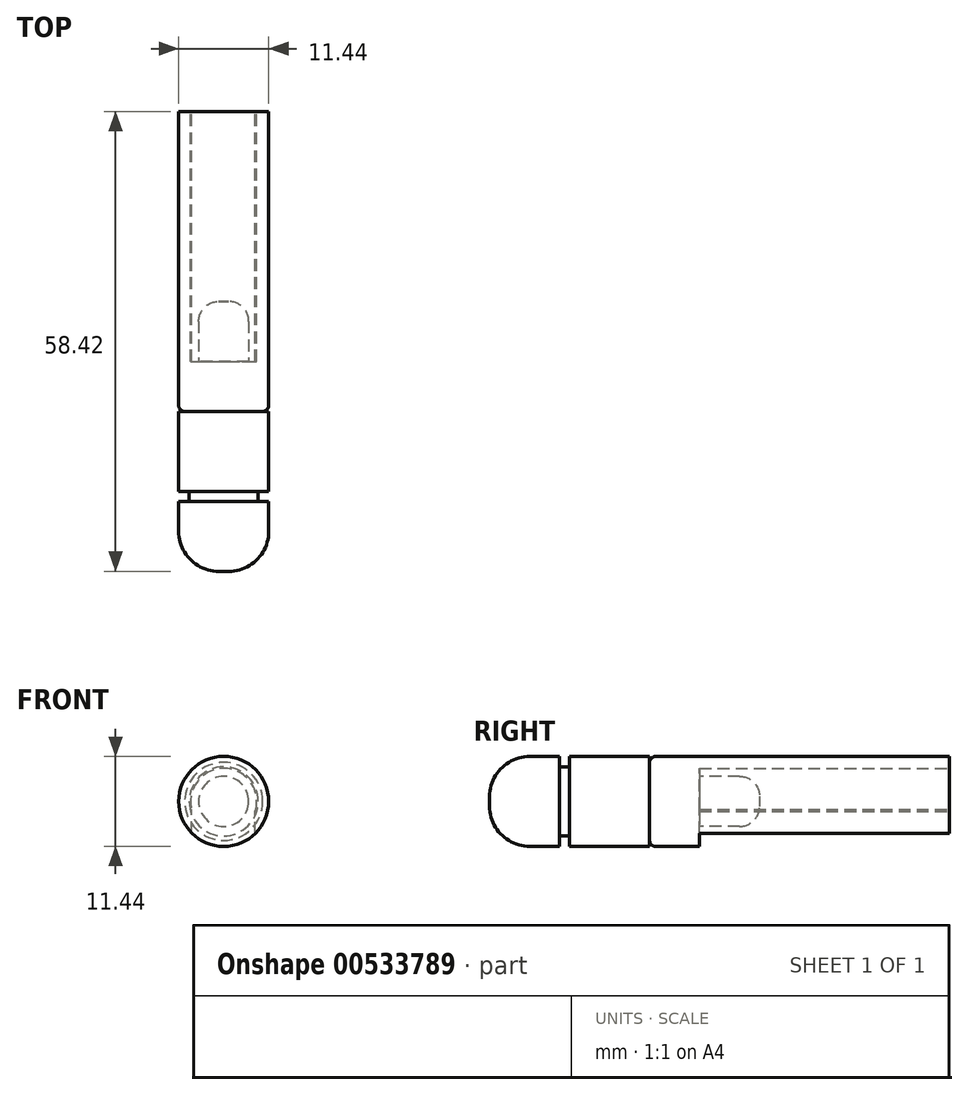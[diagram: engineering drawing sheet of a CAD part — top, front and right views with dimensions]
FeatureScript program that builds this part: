
annotation { "Feature Type Name" : "Feature", "Feature Type Description" : "" }
export const myFeature = defineFeature(function(context is Context, id is Id, definition is map)
    precondition{}
    {
        {
            var Q0;
            Q0=qCreatedBy(makeId("Front.planeOp"),FACE);
            var sketch = newSketch(context, id + "F0", { "sketchPlane" : qUnion([Q0])});
            skCircle(sketch, "E0", {"center": v(0, 0) * mm, "radius": 5.72 * mm});
            skSolve(sketch);
        }
        {
            var Q0;
            Q0=qSketchRegion(id+"F0",true);
            extrude(context, id + "F1", {"entities" : qUnion([Q0]), "depth" : 38.1 * mm, "offsetDistance" : 25.4 * mm});
        }
        {
            var Q0;
            Q0=makeQuery(id+"F1.opExtrude","CAP_FACE",FACE,{"disambiguationData":[OSD([sQuery(id+"F0.wireOp",EDGE,"E0")])],"isStart":false});
            var sketch = newSketch(context, id + "F2", { "sketchPlane" : qUnion([Q0])});
            skCircle(sketch, "E1", {"center": v(0, 0) * mm, "radius": 5.72 * mm});
            skSolve(sketch);
        }
        {
            var Q0;
            Q0=qSketchRegion(id+"F2",true);
            extrude(context, id + "F3", {"entities" : qUnion([Q0]), "depth" : 20.32 * mm, "offsetDistance" : 25.4 * mm});
        }
        {
            var Q0;
            Q0=makeQuery(id+"F1.opExtrude","CAP_EDGE",EDGE,{"disambiguationData":[OSD([sQuery(id+"F0.wireOp",EDGE,"E0")])],"isStart":false});
            fillet(context, id + "F4", {"entities" : qUnion([Q0]), "radius" : 0.76 * mm, "tangentPropagation" : true, "allowEdgeOverflow" : false});
        }
        {
            var Q0;
            Q0=makeQuery(id+"F1.opExtrude","CAP_FACE",FACE,{"disambiguationData":[OSD([sQuery(id+"F0.wireOp",EDGE,"E0")])],"isStart":true});
            var sketch = newSketch(context, id + "F5", { "sketchPlane" : qUnion([Q0])});
            skCircle(sketch, "E2", {"center": v(0, 0) * mm, "radius": 4.2 * mm});
            skSolve(sketch);
        }
        {
            var Q0;
            Q0=makeQuery(id+"F5.imprint","IMPRINT",FACE,{"disambiguationData":[TD([[makeQuery(id+"F5.imprint","IMPRINT",EDGE,{"derivedFrom":sQuery(id+"F5.wireOp",EDGE,"E2")}),1.0]])]});
            var Q1;
            Q1=sQuery(id+"F5.wireOp",EDGE,"E2");
            extrude(context, id + "F6", {"entities" : qUnion([Q0]), "operationType" : NewBodyOperationType.REMOVE, "surfaceEntities" : qUnion([Q1]), "oppositeDirection" : true, "depth" : 31.75 * mm, "offsetDistance" : 25.4 * mm});
        }
        {
            var Q0;
            Q0=qCreatedBy(makeId("Top.planeOp"),FACE);
            var sketch = newSketch(context, id + "F7", { "sketchPlane" : qUnion([Q0])});
            skLineSegment(sketch, "E3.bottom", {"start": v(-4.07, 0) * mm, "end": v(4, 0) * mm});
            skLineSegment(sketch, "E3.top", {"start": v(-4.07, -31.75) * mm, "end": v(4, -31.75) * mm});
            skLineSegment(sketch, "E3.left", {"start": v(-4.07, 0) * mm, "end": v(-4.07, -31.75) * mm});
            skLineSegment(sketch, "E3.right", {"start": v(4, 0) * mm, "end": v(4, -31.75) * mm});
            skSolve(sketch);
        }
        {
            var Q0;
            Q0=qSketchRegion(id+"F7",true);
            extrude(context, id + "F8", {"entities" : qUnion([Q0]), "operationType" : NewBodyOperationType.REMOVE, "oppositeDirection" : true, "depth" : 25.4 * mm, "offsetDistance" : 25.4 * mm});
        }
        {
            var Q0;
            Q0=makeQuery(id+"F8.boolean.opBoolean","MERGE",FACE,{"derivedFrom":[makeQuery(id+"F6.boolean.opBoolean","COPY",FACE,{"derivedFrom":makeQuery(id+"F6.opExtrude","CAP_FACE",FACE,{"disambiguationData":[OSD([sQuery(id+"F5.wireOp",EDGE,"E2")])],"isStart":false})}),makeQuery(id+"F8.opExtrude","SWEPT_FACE",FACE,{"disambiguationData":[OSD([sQuery(id+"F7.wireOp",EDGE,"E3.top")])]})]});
            var sketch = newSketch(context, id + "F9", { "sketchPlane" : qUnion([Q0])});
            skCircle(sketch, "E4", {"center": v(0, 0) * mm, "radius": 3.18 * mm});
            skSolve(sketch);
        }
        {
            var Q0;
            Q0=qSketchRegion(id+"F9",true);
            extrude(context, id + "F10", {"entities" : qUnion([Q0]), "operationType" : NewBodyOperationType.ADD, "depth" : 7.62 * mm, "offsetDistance" : 25.4 * mm, "hasSecondDirection" : true, "secondDirectionOppositeDirection" : true, "secondDirectionDepth" : 10.16 * mm});
        }
        {
            var Q0;
            Q0=makeQuery(id+"F10.opExtrude","CAP_EDGE",EDGE,{"disambiguationData":[OSD([sQuery(id+"F9.wireOp",EDGE,"E4")])],"isStart":false});
            fillet(context, id + "F11", {"entities" : qUnion([Q0]), "radius" : 2.54 * mm, "tangentPropagation" : true, "allowEdgeOverflow" : false});
        }
        {
            var Q0;
            Q0=makeQuery(id+"F3.opExtrude","CAP_EDGE",EDGE,{"disambiguationData":[OSD([sQuery(id+"F2.wireOp",EDGE,"E1")])],"isStart":false});
            fillet(context, id + "F12", {"entities" : qUnion([Q0]), "radius" : 5.08 * mm, "tangentPropagation" : true, "allowEdgeOverflow" : false});
        }
        {
            var Q0;
            Q0=qCreatedBy(makeId("Front.planeOp"),FACE);
            cPlane(context, id + "F13", {"entities" : qUnion([Q0]), "cplaneType" : CPlaneType.OFFSET, "offset" : 48.26 * mm, "width" : 152.4 * mm, "height" : 152.4 * mm});
        }
        {
            var Q0;
            Q0=qCreatedBy(id+"F13.planeOp",FACE);
            var sketch = newSketch(context, id + "F14", { "sketchPlane" : qUnion([Q0])});
            skCircle(sketch, "E5", {"center": v(0, 0) * mm, "radius": 10.19 * mm});
            skCircle(sketch, "E6", {"center": v(0, 0) * mm, "radius": 4.39 * mm});
            skSolve(sketch);
        }
        {
            var Q0;
            Q0=makeQuery(id+"F14.imprint","IMPRINT",FACE,{"disambiguationData":[TD([[makeQuery(id+"F14.imprint","IMPRINT",EDGE,{"derivedFrom":sQuery(id+"F14.wireOp",EDGE,"E5")}),1.0]])]});
            extrude(context, id + "F15", {"entities" : qUnion([Q0]), "operationType" : NewBodyOperationType.REMOVE, "depth" : 1.27 * mm, "offsetDistance" : 25.4 * mm});
        }
    });
